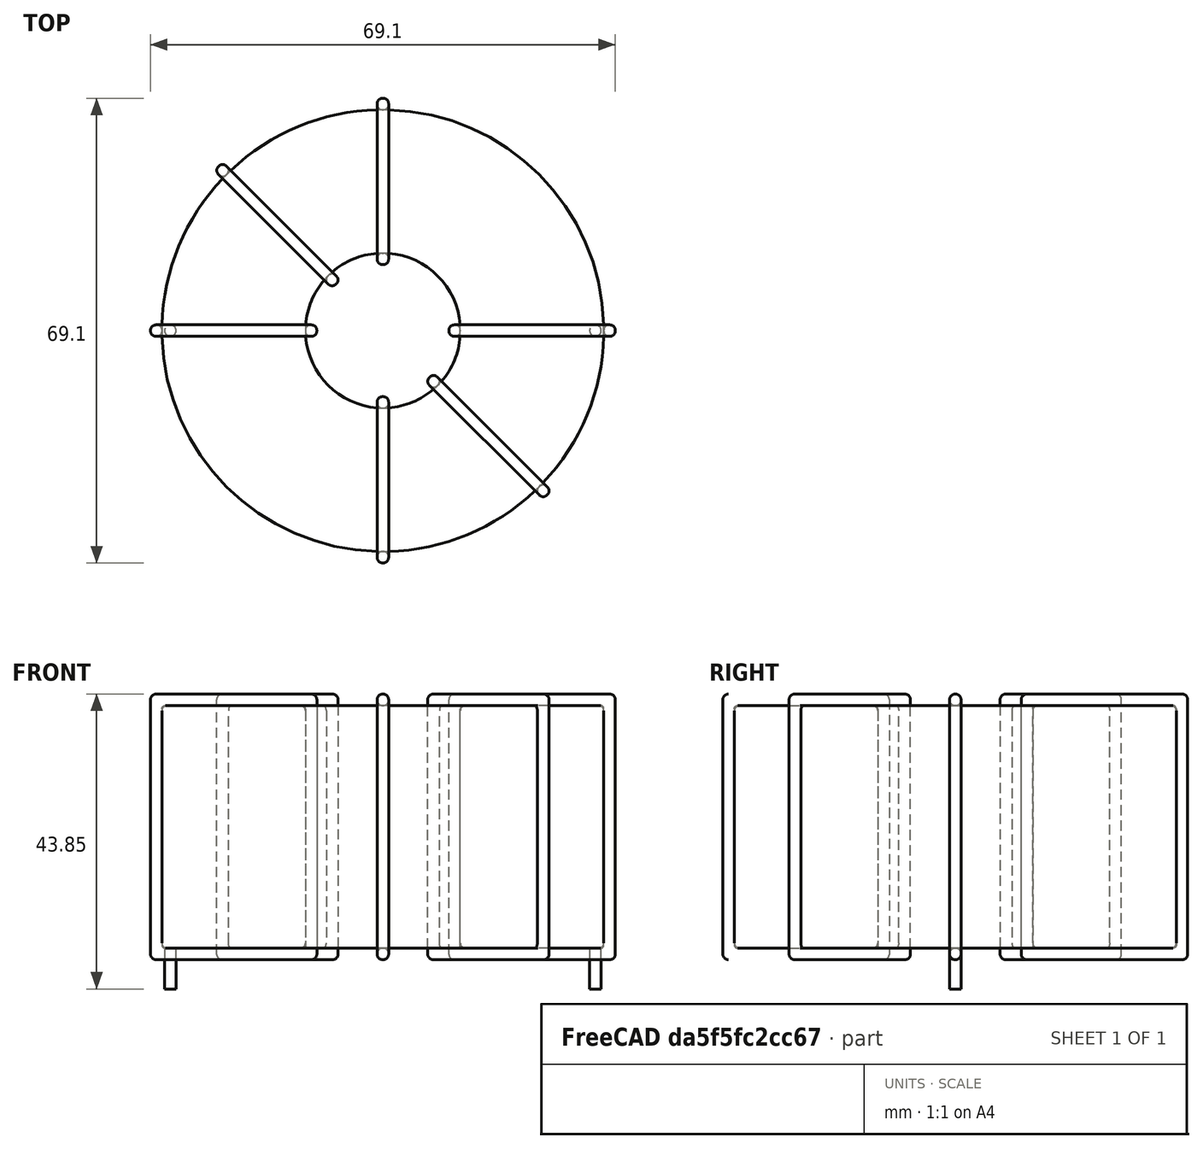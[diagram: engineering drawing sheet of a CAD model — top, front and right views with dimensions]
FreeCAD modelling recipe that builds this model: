
FCSTD DOCUMENT  (FreeCAD 0.16R6703 (Git))
Label: L_Radial_round_toroid_horizontal_master
License: All rights reserved
LicenseURL: http://en.wikipedia.org/wiki/All_rights_reserved
objects: Sketcher::SketchObject×6, PartDesign::Pad×6, PartDesign::Fillet×5, Spreadsheet::Sheet×1
note: 23 computed .brp shape members not serialized (recipe doc carries the construction recipe); baked Part::Feature solids carry a one-line shape summary decoded from their .brp

FEATURE [Spreadsheet::Sheet] Spreadsheet  label="dimensions"
  cells = A1=Wx; B1(Wx)=69.09999999999999; C1(WW)=23.03333333333333; A2=Wy; B2(Wy)=69.09999999999999; A3=RM; B3(RMx)=63.2; C3(RMy)=0; A4=d_wire; B4(d_wire)=1.7; A5=H; B5(H)=36.1; A6=offsetx; B6(offsetx)=2.949999999999996
FEATURE [Sketcher::SketchObject] Sketch
  Placement = pos=(0,0,2.2) rot=(0,0,1;0rad)
  expr: Placement.Base.z = 0.5 + Spreadsheet.d_wire
  expr: Constraints[0] = Spreadsheet.Wx / 2 - Spreadsheet.d_wire
  expr: Constraints[4] = Spreadsheet.WW / 2
  expr: Constraints[2] = Spreadsheet.RMy / 2
  expr: Constraints[1] = Spreadsheet.RMx / 2
  sketch-geometry (2):
    g0: Circle CenterX=31.6 CenterY=0 CenterZ=0 NormalX=0 NormalY=0 NormalZ=1 Radius=32.85
    g1: Circle CenterX=31.6 CenterY=0 CenterZ=0 NormalX=0 NormalY=0 NormalZ=1 Radius=11.5167
  constraints (5):
    c: Radius(g0) = 32.85
    c: DistanceX(g-1,g0) = 31.6
    c: DistanceY(g-1,g0) = 0
    c: Coincident(g1,g0)
    c: Radius(g1) = 11.5167
FEATURE [PartDesign::Pad] Pad
  Length = 36.1
  Length2 = 100
  Placement = pos=(0,0,2.2) rot=(0,0,1;0rad)
  Sketch = -> Sketch
  Type = 0
  expr: Length = Spreadsheet.H
FEATURE [Sketcher::SketchObject] Sketch001
  Placement = pos=(0,0,1.35) rot=(0,0,1;0rad)
  expr: Placement.Base.z = 0.5 + Spreadsheet.d_wire * 0.5
  expr: Constraints[4] = Spreadsheet.RMx
  expr: Constraints[2] = Spreadsheet.RMy
  expr: Constraints[1] = Spreadsheet.d_wire / 2
  sketch-geometry (2):
    g0: Circle CenterX=0 CenterY=0 CenterZ=0 NormalX=0 NormalY=0 NormalZ=1 Radius=0.85
    g1: Circle CenterX=63.2 CenterY=0 CenterZ=0 NormalX=0 NormalY=0 NormalZ=1 Radius=0.85
  constraints (5):
    c: Equal(g0,g1)
    c: Radius(g0) = 0.85
    c: DistanceY(g-1,g1) = 0
    c: Coincident(g0,g-1)
    c: DistanceX(g-1,g1) = 63.2
FEATURE [PartDesign::Pad] Pad001
  Length = 0.85
  Length2 = 5.2
  Placement = pos=(0,0,1.35) rot=(0,0,1;0rad)
  Reversed = true
  Sketch = -> Sketch001
  Type = 4
  expr: Length2 = 3.5 + Spreadsheet.d_wire
  expr: Length = Spreadsheet.d_wire / 2
FEATURE [PartDesign::Fillet] Fillet
  Base = -> Pad [Edge6,Edge3,Edge2]
  Placement = pos=(0,0,2.2) rot=(0,0,1;0rad)
  Radius = 0.5
FEATURE [Sketcher::SketchObject] Sketch003
  Placement = pos=(31.6,0,0) rot=(1,0,0;1.5708rad)
  expr: Placement.Base.x = Spreadsheet.RMx / 2
  expr: Constraints[49] = Spreadsheet.Wx - Spreadsheet.d_wire * 2
  expr: Constraints[44] = Spreadsheet.d_wire
  expr: Constraints[23] = Spreadsheet.H
  expr: Constraints[22] = Spreadsheet.Wx / 2 - Spreadsheet.d_wire
  expr: Placement.Base.y = Spreadsheet.RMy / 2
  expr: Constraints[21] = (Spreadsheet.Wx - Spreadsheet.WW) / 2 - Spreadsheet.d_wire
  expr: Constraints[19] = Spreadsheet.d_wire
  expr: Constraints[17] = Spreadsheet.d_wire
  expr: Constraints[18] = Spreadsheet.d_wire
  expr: Constraints[16] = Spreadsheet.d_wire
  sketch-geometry (16):
    g0: LineSegment StartX=-9.81667 StartY=0.5 StartZ=0 EndX=-34.55 EndY=0.5 EndZ=0
    g1: LineSegment StartX=-34.55 StartY=0.5 StartZ=0 EndX=-34.55 EndY=40 EndZ=0
    g2: LineSegment StartX=-34.55 StartY=40 StartZ=0 EndX=-9.81667 EndY=40 EndZ=0
    g3: LineSegment StartX=-9.81667 StartY=40 StartZ=0 EndX=-9.81667 EndY=0.5 EndZ=0
    g4: LineSegment StartX=-32.85 StartY=38.3 StartZ=0 EndX=-11.5167 EndY=38.3 EndZ=0
    g5: LineSegment StartX=-11.5167 StartY=38.3 StartZ=0 EndX=-11.5167 EndY=2.2 EndZ=0
    g6: LineSegment StartX=-11.5167 StartY=2.2 StartZ=0 EndX=-32.85 EndY=2.2 EndZ=0
    g7: LineSegment StartX=-32.85 StartY=2.2 StartZ=0 EndX=-32.85 EndY=38.3 EndZ=0
    g8: LineSegment StartX=9.81667 StartY=40 StartZ=0 EndX=34.55 EndY=40 EndZ=0
    g9: LineSegment StartX=34.55 StartY=40 StartZ=0 EndX=34.55 EndY=0.5 EndZ=0
    g10: LineSegment StartX=34.55 StartY=0.5 StartZ=0 EndX=9.81667 EndY=0.5 EndZ=0
    g11: LineSegment StartX=9.81667 StartY=0.5 StartZ=0 EndX=9.81667 EndY=40 EndZ=0
    g12: LineSegment StartX=11.5167 StartY=38.3 StartZ=0 EndX=32.85 EndY=38.3 EndZ=0
    g13: LineSegment StartX=32.85 StartY=38.3 StartZ=0 EndX=32.85 EndY=2.2 EndZ=0
    g14: LineSegment StartX=32.85 StartY=2.2 StartZ=0 EndX=11.5167 EndY=2.2 EndZ=0
    g15: LineSegment StartX=11.5167 StartY=2.2 StartZ=0 EndX=11.5167 EndY=38.3 EndZ=0
  constraints (50):
    c: Horizontal(g0)
    c: Coincident(g1,g0)
    c: Vertical(g1)
    c: Coincident(g2,g1)
    c: Horizontal(g2)
    c: Coincident(g3,g2)
    c: Coincident(g3,g0)
    c: Vertical(g3)
    c: Coincident(g4,g5)
    c: Coincident(g5,g6)
    c: Coincident(g6,g7)
    c: Coincident(g7,g4)
    c: Horizontal(g4)
    c: Horizontal(g6)
    c: Vertical(g5)
    c: Vertical(g7)
    c: DistanceX(g1,g4) = 1.7
    c: DistanceY(g4,g1) = 1.7
    c: DistanceX(g5,g0) = 1.7
    c: DistanceY(g0,g5) = 1.7
    c: DistanceY(g-1,g0) = 0.5
    c: DistanceX(g6,g6) = 21.3333
    c: DistanceX(g6,g-1) = 32.85
    c: DistanceY(g7,g7) = 36.1
    c: Coincident(g8,g9)
    c: Coincident(g9,g10)
    c: Coincident(g10,g11)
    c: Coincident(g11,g8)
    c: Horizontal(g8)
    c: Horizontal(g10)
    c: Vertical(g9)
    c: Vertical(g11)
    c: Coincident(g12,g13)
    c: Coincident(g13,g14)
    c: Coincident(g14,g15)
    c: Coincident(g15,g12)
    c: Horizontal(g12)
    c: Horizontal(g14)
    c: Vertical(g13)
    c: Vertical(g15)
    c: DistanceY(g8,g2) = 0
    c: DistanceY(g10,g0) = 0
    c: DistanceY(g14,g5) = 0
    c: DistanceY(g12,g4) = 0
    c: DistanceX(g8,g12) = 1.7
    c: Equal(g8,g2)
    c: Equal(g12,g4)
    c: Equal(g9,g1)
    c: Equal(g13,g7)
    c: DistanceX(g4,g12) = 65.7
FEATURE [PartDesign::Pad] Pad002
  Length = 1.7
  Length2 = 100
  Midplane = true
  Placement = pos=(31.6,0,0) rot=(1,0,0;1.5708rad)
  Sketch = -> Sketch003
  Type = 0
  expr: Length = Spreadsheet.d_wire
FEATURE [PartDesign::Fillet] Fillet001
  Base = -> Pad002 [Edge38,Edge41,Edge42,Edge43,Edge29,Edge32,Edge33,Edge34,Edge25,Edge35,Edge36,Edge13,Edge14,Edge15,Edge16,Edge17,Edge18,Edge19,Edge1,Edge2,Edge3,Edge4,Edge5,Edge6,Edge7,Edge37,Edge39,Edge40,Edge20,Edge23,Edge24,Edge21,Edge22,Edge8,Edge9,Edge10,Edge11,Edge12,Edge26,Edge27,+8 more]
  Placement = pos=(31.6,0,0) rot=(1,0,0;1.5708rad)
  Radius = 0.799
  expr: Radius = Spreadsheet.d_wire * 0.47
FEATURE [Sketcher::SketchObject] Sketch004
  Placement = pos=(31.6,0,0) rot=(0.862856,0.357407,0.357407;1.71777rad)
  expr: Placement.Base.x = Spreadsheet.RMx / 2
  expr: Constraints[49] = Spreadsheet.Wx - 2 * Spreadsheet.d_wire
  expr: Constraints[44] = Spreadsheet.d_wire
  expr: Constraints[23] = Spreadsheet.H
  expr: Constraints[22] = Spreadsheet.Wx / 2 - Spreadsheet.d_wire
  expr: Placement.Base.y = Spreadsheet.RMy / 2
  expr: Constraints[21] = (Spreadsheet.Wx - Spreadsheet.WW) / 2 - Spreadsheet.d_wire
  expr: Constraints[19] = Spreadsheet.d_wire
  expr: Constraints[17] = Spreadsheet.d_wire
  expr: Constraints[18] = Spreadsheet.d_wire
  expr: Constraints[16] = Spreadsheet.d_wire
  sketch-geometry (16):
    g0: LineSegment StartX=-9.81667 StartY=0.5 StartZ=0 EndX=-34.55 EndY=0.5 EndZ=0
    g1: LineSegment StartX=-34.55 StartY=0.5 StartZ=0 EndX=-34.55 EndY=40 EndZ=0
    g2: LineSegment StartX=-34.55 StartY=40 StartZ=0 EndX=-9.81667 EndY=40 EndZ=0
    g3: LineSegment StartX=-9.81667 StartY=40 StartZ=0 EndX=-9.81667 EndY=0.5 EndZ=0
    g4: LineSegment StartX=-32.85 StartY=38.3 StartZ=0 EndX=-11.5167 EndY=38.3 EndZ=0
    g5: LineSegment StartX=-11.5167 StartY=38.3 StartZ=0 EndX=-11.5167 EndY=2.2 EndZ=0
    g6: LineSegment StartX=-11.5167 StartY=2.2 StartZ=0 EndX=-32.85 EndY=2.2 EndZ=0
    g7: LineSegment StartX=-32.85 StartY=2.2 StartZ=0 EndX=-32.85 EndY=38.3 EndZ=0
    g8: LineSegment StartX=9.81667 StartY=40 StartZ=0 EndX=34.55 EndY=40 EndZ=0
    g9: LineSegment StartX=34.55 StartY=40 StartZ=0 EndX=34.55 EndY=0.5 EndZ=0
    g10: LineSegment StartX=34.55 StartY=0.5 StartZ=0 EndX=9.81667 EndY=0.5 EndZ=0
    g11: LineSegment StartX=9.81667 StartY=0.5 StartZ=0 EndX=9.81667 EndY=40 EndZ=0
    g12: LineSegment StartX=11.5167 StartY=38.3 StartZ=0 EndX=32.85 EndY=38.3 EndZ=0
    g13: LineSegment StartX=32.85 StartY=38.3 StartZ=0 EndX=32.85 EndY=2.2 EndZ=0
    g14: LineSegment StartX=32.85 StartY=2.2 StartZ=0 EndX=11.5167 EndY=2.2 EndZ=0
    g15: LineSegment StartX=11.5167 StartY=2.2 StartZ=0 EndX=11.5167 EndY=38.3 EndZ=0
  constraints (50):
    c: Horizontal(g0)
    c: Coincident(g1,g0)
    c: Vertical(g1)
    c: Coincident(g2,g1)
    c: Horizontal(g2)
    c: Coincident(g3,g2)
    c: Coincident(g3,g0)
    c: Vertical(g3)
    c: Coincident(g4,g5)
    c: Coincident(g5,g6)
    c: Coincident(g6,g7)
    c: Coincident(g7,g4)
    c: Horizontal(g4)
    c: Horizontal(g6)
    c: Vertical(g5)
    c: Vertical(g7)
    c: DistanceX(g1,g4) = 1.7
    c: DistanceY(g4,g1) = 1.7
    c: DistanceX(g5,g0) = 1.7
    c: DistanceY(g0,g5) = 1.7
    c: DistanceY(g-1,g0) = 0.5
    c: DistanceX(g6,g6) = 21.3333
    c: DistanceX(g6,g-1) = 32.85
    c: DistanceY(g7,g7) = 36.1
    c: Coincident(g8,g9)
    c: Coincident(g9,g10)
    c: Coincident(g10,g11)
    c: Coincident(g11,g8)
    c: Horizontal(g8)
    c: Horizontal(g10)
    c: Vertical(g9)
    c: Vertical(g11)
    c: Coincident(g12,g13)
    c: Coincident(g13,g14)
    c: Coincident(g14,g15)
    c: Coincident(g15,g12)
    c: Horizontal(g12)
    c: Horizontal(g14)
    c: Vertical(g13)
    c: Vertical(g15)
    c: DistanceY(g8,g2) = 0
    c: DistanceY(g10,g0) = 0
    c: DistanceY(g14,g5) = 0
    c: DistanceY(g12,g4) = 0
    c: DistanceX(g8,g12) = 1.7
    c: Equal(g8,g2)
    c: Equal(g12,g4)
    c: Equal(g9,g1)
    c: Equal(g13,g7)
    c: DistanceX(g4,g12) = 65.7
FEATURE [PartDesign::Pad] Pad003
  Length = 1.7
  Length2 = 100
  Midplane = true
  Placement = pos=(31.6,0,0) rot=(0.862856,0.357407,0.357407;1.71777rad)
  Sketch = -> Sketch004
  Type = 0
  expr: Length = Spreadsheet.d_wire
FEATURE [PartDesign::Fillet] Fillet002
  Base = -> Pad003 [Edge38,Edge41,Edge42,Edge43,Edge29,Edge32,Edge33,Edge34,Edge25,Edge35,Edge36,Edge13,Edge14,Edge15,Edge16,Edge17,Edge18,Edge19,Edge1,Edge2,Edge3,Edge4,Edge5,Edge6,Edge7,Edge37,Edge39,Edge40,Edge20,Edge23,Edge24,Edge21,Edge22,Edge8,Edge9,Edge10,Edge11,Edge12,Edge26,Edge27,+8 more]
  Placement = pos=(31.6,0,0) rot=(0.862856,0.357407,0.357407;1.71777rad)
  Radius = 0.799
  expr: Radius = Spreadsheet.d_wire * 0.47
FEATURE [Sketcher::SketchObject] Sketch005
  Placement = pos=(31.6,0,0) rot=(0.862856,-0.357407,-0.357407;1.71777rad)
  expr: Placement.Base.x = Spreadsheet.RMx / 2
  expr: Constraints[49] = Spreadsheet.Wx - 2 * Spreadsheet.d_wire
  expr: Constraints[44] = Spreadsheet.d_wire
  expr: Constraints[23] = Spreadsheet.H
  expr: Constraints[22] = Spreadsheet.Wx / 2 - Spreadsheet.d_wire
  expr: Placement.Base.y = Spreadsheet.RMy / 2
  expr: Constraints[21] = (Spreadsheet.Wx - Spreadsheet.WW) / 2 - Spreadsheet.d_wire
  expr: Constraints[19] = Spreadsheet.d_wire
  expr: Constraints[17] = Spreadsheet.d_wire
  expr: Constraints[18] = Spreadsheet.d_wire
  expr: Constraints[16] = Spreadsheet.d_wire
  sketch-geometry (16):
    g0: LineSegment StartX=-9.81667 StartY=0.5 StartZ=0 EndX=-34.55 EndY=0.5 EndZ=0
    g1: LineSegment StartX=-34.55 StartY=0.5 StartZ=0 EndX=-34.55 EndY=40 EndZ=0
    g2: LineSegment StartX=-34.55 StartY=40 StartZ=0 EndX=-9.81667 EndY=40 EndZ=0
    g3: LineSegment StartX=-9.81667 StartY=40 StartZ=0 EndX=-9.81667 EndY=0.5 EndZ=0
    g4: LineSegment StartX=-32.85 StartY=38.3 StartZ=0 EndX=-11.5167 EndY=38.3 EndZ=0
    g5: LineSegment StartX=-11.5167 StartY=38.3 StartZ=0 EndX=-11.5167 EndY=2.2 EndZ=0
    g6: LineSegment StartX=-11.5167 StartY=2.2 StartZ=0 EndX=-32.85 EndY=2.2 EndZ=0
    g7: LineSegment StartX=-32.85 StartY=2.2 StartZ=0 EndX=-32.85 EndY=38.3 EndZ=0
    g8: LineSegment StartX=9.81667 StartY=40 StartZ=0 EndX=34.55 EndY=40 EndZ=0
    g9: LineSegment StartX=34.55 StartY=40 StartZ=0 EndX=34.55 EndY=0.5 EndZ=0
    g10: LineSegment StartX=34.55 StartY=0.5 StartZ=0 EndX=9.81667 EndY=0.5 EndZ=0
    g11: LineSegment StartX=9.81667 StartY=0.5 StartZ=0 EndX=9.81667 EndY=40 EndZ=0
    g12: LineSegment StartX=11.5167 StartY=38.3 StartZ=0 EndX=32.85 EndY=38.3 EndZ=0
    g13: LineSegment StartX=32.85 StartY=38.3 StartZ=0 EndX=32.85 EndY=2.2 EndZ=0
    g14: LineSegment StartX=32.85 StartY=2.2 StartZ=0 EndX=11.5167 EndY=2.2 EndZ=0
    g15: LineSegment StartX=11.5167 StartY=2.2 StartZ=0 EndX=11.5167 EndY=38.3 EndZ=0
  constraints (50):
    c: Horizontal(g0)
    c: Coincident(g1,g0)
    c: Vertical(g1)
    c: Coincident(g2,g1)
    c: Horizontal(g2)
    c: Coincident(g3,g2)
    c: Coincident(g3,g0)
    c: Vertical(g3)
    c: Coincident(g4,g5)
    c: Coincident(g5,g6)
    c: Coincident(g6,g7)
    c: Coincident(g7,g4)
    c: Horizontal(g4)
    c: Horizontal(g6)
    c: Vertical(g5)
    c: Vertical(g7)
    c: DistanceX(g1,g4) = 1.7
    c: DistanceY(g4,g1) = 1.7
    c: DistanceX(g5,g0) = 1.7
    c: DistanceY(g0,g5) = 1.7
    c: DistanceY(g-1,g0) = 0.5
    c: DistanceX(g6,g6) = 21.3333
    c: DistanceX(g6,g-1) = 32.85
    c: DistanceY(g7,g7) = 36.1
    c: Coincident(g8,g9)
    c: Coincident(g9,g10)
    c: Coincident(g10,g11)
    c: Coincident(g11,g8)
    c: Horizontal(g8)
    c: Horizontal(g10)
    c: Vertical(g9)
    c: Vertical(g11)
    c: Coincident(g12,g13)
    c: Coincident(g13,g14)
    c: Coincident(g14,g15)
    c: Coincident(g15,g12)
    c: Horizontal(g12)
    c: Horizontal(g14)
    c: Vertical(g13)
    c: Vertical(g15)
    c: DistanceY(g8,g2) = 0
    c: DistanceY(g10,g0) = 0
    c: DistanceY(g14,g5) = 0
    c: DistanceY(g12,g4) = 0
    c: DistanceX(g8,g12) = 1.7
    c: Equal(g8,g2)
    c: Equal(g12,g4)
    c: Equal(g9,g1)
    c: Equal(g13,g7)
    c: DistanceX(g4,g12) = 65.7
FEATURE [PartDesign::Pad] Pad004
  Length = 1.7
  Length2 = 100
  Midplane = true
  Placement = pos=(31.6,0,0) rot=(0.862856,-0.357407,-0.357407;1.71777rad)
  Sketch = -> Sketch005
  Type = 0
  expr: Length = Spreadsheet.d_wire
FEATURE [PartDesign::Fillet] Fillet003
  Base = -> Pad004 [Edge38,Edge41,Edge42,Edge43,Edge29,Edge32,Edge33,Edge34,Edge25,Edge35,Edge36,Edge13,Edge14,Edge15,Edge16,Edge17,Edge18,Edge19,Edge1,Edge2,Edge3,Edge4,Edge5,Edge6,Edge7,Edge37,Edge39,Edge40,Edge20,Edge23,Edge24,Edge21,Edge22,Edge8,Edge9,Edge10,Edge11,Edge12,Edge26,Edge27,+8 more]
  Placement = pos=(31.6,0,0) rot=(0.862856,-0.357407,-0.357407;1.71777rad)
  Radius = 0.799
  expr: Radius = Spreadsheet.d_wire * 0.47
FEATURE [Sketcher::SketchObject] Sketch006
  Placement = pos=(31.6,0,0) rot=(0.57735,0.57735,0.57735;2.0944rad)
  expr: Placement.Base.x = Spreadsheet.RMx / 2
  expr: Constraints[49] = Spreadsheet.Wx - Spreadsheet.d_wire * 2
  expr: Constraints[44] = Spreadsheet.d_wire
  expr: Constraints[23] = Spreadsheet.H
  expr: Constraints[22] = Spreadsheet.Wx / 2 - Spreadsheet.d_wire
  expr: Placement.Base.y = Spreadsheet.RMy / 2
  expr: Constraints[21] = (Spreadsheet.Wx - Spreadsheet.WW) / 2 - Spreadsheet.d_wire
  expr: Constraints[19] = Spreadsheet.d_wire
  expr: Constraints[17] = Spreadsheet.d_wire
  expr: Constraints[18] = Spreadsheet.d_wire
  expr: Constraints[16] = Spreadsheet.d_wire
  sketch-geometry (16):
    g0: LineSegment StartX=-9.81667 StartY=0.5 StartZ=0 EndX=-34.55 EndY=0.5 EndZ=0
    g1: LineSegment StartX=-34.55 StartY=0.5 StartZ=0 EndX=-34.55 EndY=40 EndZ=0
    g2: LineSegment StartX=-34.55 StartY=40 StartZ=0 EndX=-9.81667 EndY=40 EndZ=0
    g3: LineSegment StartX=-9.81667 StartY=40 StartZ=0 EndX=-9.81667 EndY=0.5 EndZ=0
    g4: LineSegment StartX=-32.85 StartY=38.3 StartZ=0 EndX=-11.5167 EndY=38.3 EndZ=0
    g5: LineSegment StartX=-11.5167 StartY=38.3 StartZ=0 EndX=-11.5167 EndY=2.2 EndZ=0
    g6: LineSegment StartX=-11.5167 StartY=2.2 StartZ=0 EndX=-32.85 EndY=2.2 EndZ=0
    g7: LineSegment StartX=-32.85 StartY=2.2 StartZ=0 EndX=-32.85 EndY=38.3 EndZ=0
    g8: LineSegment StartX=9.81667 StartY=40 StartZ=0 EndX=34.55 EndY=40 EndZ=0
    g9: LineSegment StartX=34.55 StartY=40 StartZ=0 EndX=34.55 EndY=0.5 EndZ=0
    g10: LineSegment StartX=34.55 StartY=0.5 StartZ=0 EndX=9.81667 EndY=0.5 EndZ=0
    g11: LineSegment StartX=9.81667 StartY=0.5 StartZ=0 EndX=9.81667 EndY=40 EndZ=0
    g12: LineSegment StartX=11.5167 StartY=38.3 StartZ=0 EndX=32.85 EndY=38.3 EndZ=0
    g13: LineSegment StartX=32.85 StartY=38.3 StartZ=0 EndX=32.85 EndY=2.2 EndZ=0
    g14: LineSegment StartX=32.85 StartY=2.2 StartZ=0 EndX=11.5167 EndY=2.2 EndZ=0
    g15: LineSegment StartX=11.5167 StartY=2.2 StartZ=0 EndX=11.5167 EndY=38.3 EndZ=0
  constraints (50):
    c: Horizontal(g0)
    c: Coincident(g1,g0)
    c: Vertical(g1)
    c: Coincident(g2,g1)
    c: Horizontal(g2)
    c: Coincident(g3,g2)
    c: Coincident(g3,g0)
    c: Vertical(g3)
    c: Coincident(g4,g5)
    c: Coincident(g5,g6)
    c: Coincident(g6,g7)
    c: Coincident(g7,g4)
    c: Horizontal(g4)
    c: Horizontal(g6)
    c: Vertical(g5)
    c: Vertical(g7)
    c: DistanceX(g1,g4) = 1.7
    c: DistanceY(g4,g1) = 1.7
    c: DistanceX(g5,g0) = 1.7
    c: DistanceY(g0,g5) = 1.7
    c: DistanceY(g-1,g0) = 0.5
    c: DistanceX(g6,g6) = 21.3333
    c: DistanceX(g6,g-1) = 32.85
    c: DistanceY(g7,g7) = 36.1
    c: Coincident(g8,g9)
    c: Coincident(g9,g10)
    c: Coincident(g10,g11)
    c: Coincident(g11,g8)
    c: Horizontal(g8)
    c: Horizontal(g10)
    c: Vertical(g9)
    c: Vertical(g11)
    c: Coincident(g12,g13)
    c: Coincident(g13,g14)
    c: Coincident(g14,g15)
    c: Coincident(g15,g12)
    c: Horizontal(g12)
    c: Horizontal(g14)
    c: Vertical(g13)
    c: Vertical(g15)
    c: DistanceY(g8,g2) = 0
    c: DistanceY(g10,g0) = 0
    c: DistanceY(g14,g5) = 0
    c: DistanceY(g12,g4) = 0
    c: DistanceX(g8,g12) = 1.7
    c: Equal(g8,g2)
    c: Equal(g12,g4)
    c: Equal(g9,g1)
    c: Equal(g13,g7)
    c: DistanceX(g4,g12) = 65.7
FEATURE [PartDesign::Pad] Pad005
  Length = 1.7
  Length2 = 100
  Midplane = true
  Placement = pos=(31.6,0,0) rot=(0.57735,0.57735,0.57735;2.0944rad)
  Sketch = -> Sketch006
  Type = 0
  expr: Length = Spreadsheet.d_wire
FEATURE [PartDesign::Fillet] Fillet004
  Base = -> Pad005 [Edge38,Edge41,Edge42,Edge43,Edge29,Edge32,Edge33,Edge34,Edge25,Edge35,Edge36,Edge13,Edge14,Edge15,Edge16,Edge17,Edge18,Edge19,Edge1,Edge2,Edge3,Edge4,Edge5,Edge6,Edge7,Edge37,Edge39,Edge40,Edge20,Edge23,Edge24,Edge21,Edge22,Edge8,Edge9,Edge10,Edge11,Edge12,Edge26,Edge27,+8 more]
  Placement = pos=(31.6,0,0) rot=(0.57735,0.57735,0.57735;2.0944rad)
  Radius = 0.799
  expr: Radius = Spreadsheet.d_wire * 0.47
